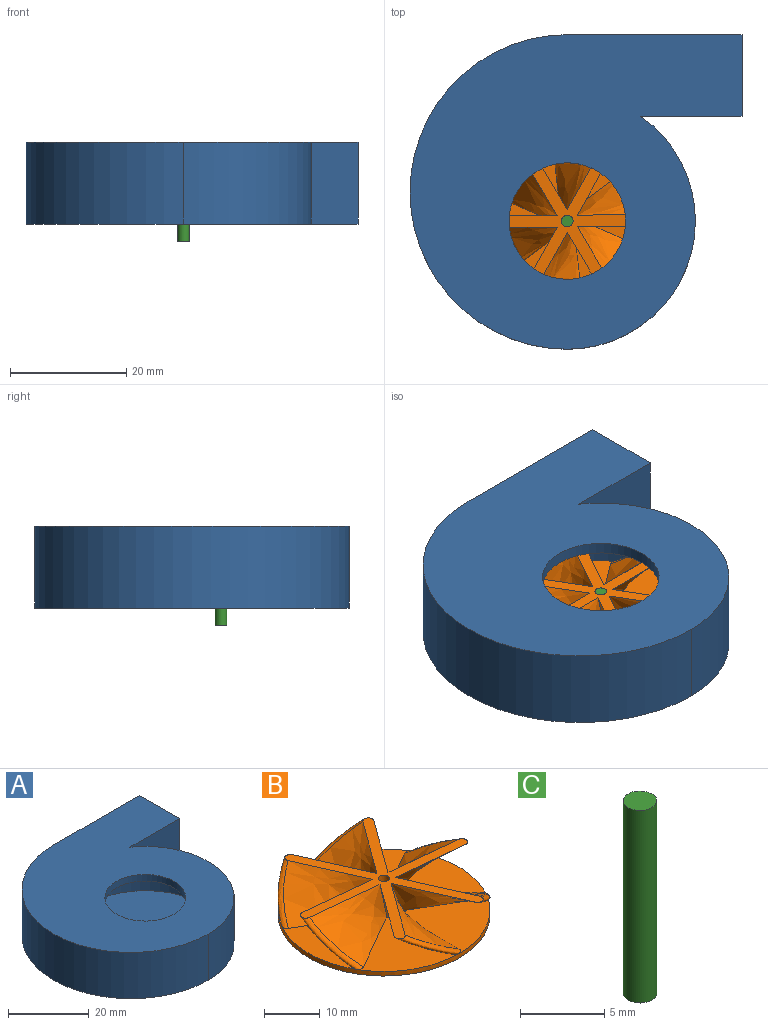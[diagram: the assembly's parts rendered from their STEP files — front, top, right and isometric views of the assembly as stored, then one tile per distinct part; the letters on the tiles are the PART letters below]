
ASSEMBLY  parts=3 mates=3
PART A: 15 faces, bbox 57x54x14 mm
  f0: plane 14x14mm, normal (1,0,0), area 96mm2, adj f2,f5,f6,f7,f8,f9,f12,f13
  f1: cylinder r=2mm len=4mm, axis (0,0,-1), area 25.1mm2, adj f7,f13
  f2: plane 30x14mm, normal (0,1,0), area 420mm2, adj f0,f3,f6,f7
  f3: cylinder r=27mm len=54mm, axis (0,0,-1), area 1187.5mm2, adj f2,f4,f6,f7
  f4: cylinder r=22mm len=40mm, axis (0,0,-1), area 778.9mm2, adj f3,f5,f6,f7
  f5: plane 17.35x14mm, normal (0,-1,0), area 242.9mm2, adj f0,f4,f6,f7
  f6: plane 57x54mm, normal (0,0,1), area 1976.8mm2, adj f0,f2,f3,f4,f5,f14
  f7: plane 57x54mm, normal (0,0,-1), area 2278.4mm2, adj f0,f1,f2,f3,f4,f5
  f8: plane 30x10mm, normal (0,1,0), area 300mm2, adj f0,f11,f12,f13
  f9: plane 30x10mm, normal (0,-1,0), area 300mm2, adj f0,f10,f12,f13
  f10: cylinder r=25mm len=50mm, axis (0,0,-1), area 785.4mm2, adj f9,f11,f12,f13
  f11: cylinder r=20mm len=40mm, axis (0,0,-1), area 628.3mm2, adj f8,f10,f12,f13
  f12: plane 55x50mm, normal (0,0,-1), area 1595.9mm2, adj f0,f8,f9,f10,f11,f14
  f13: plane 55x50mm, normal (0,0,1), area 1897.5mm2, adj f0,f1,f8,f9,f10,f11
  f14: cylinder r=10mm len=20mm, axis (0,0,-1), area 125.7mm2, adj f6,f12
PART B: 29 faces, bbox 38.3x40.7x11.3 mm
  f0: bspline ~16.86x15.64mm, area 156.6mm2, adj f1,f17,f18,f21
  f1: bspline ~12.86x7mm, area 32.7mm2, adj f0,f2,f18,f20,f21
  f2: bspline ~17.41x15.51mm, area 156.5mm2, adj f1,f3,f18,f20
  f3: bspline ~17.7x13.7mm, area 156.6mm2, adj f2,f4,f18,f20
  f4: bspline ~17.26x10mm, area 32.7mm2, adj f3,f5,f18,f20,f25
  f5: bspline ~16.5x14.45mm, area 156.5mm2, adj f4,f6,f18,f25
  f6: bspline ~15.3x15.12mm, area 156.6mm2, adj f5,f7,f18,f25
  f7: bspline ~10.15x9.3mm, area 32.7mm2, adj f6,f8,f18,f24,f25
  f8: bspline ~17.65x14.84mm, area 156.5mm2, adj f7,f9,f18,f24
  f9: bspline ~16.86x15.64mm, area 156.6mm2, adj f8,f10,f18,f24
  f10: bspline ~12.86x7mm, area 32.7mm2, adj f9,f11,f18,f23,f24
  f11: bspline ~17.41x15.51mm, area 156.5mm2, adj f10,f12,f18,f23
  f12: bspline ~17.7x13.7mm, area 156.6mm2, adj f11,f13,f18,f23
  f13: bspline ~17.26x10mm, area 32.7mm2, adj f12,f14,f18,f22,f23
  f14: bspline ~16.5x14.45mm, area 156.5mm2, adj f13,f15,f18,f22
  f15: bspline ~15.3x15.12mm, area 156.6mm2, adj f14,f16,f18,f22
  f16: bspline ~10.15x9.3mm, area 32.7mm2, adj f15,f17,f18,f21,f22
  f17: bspline ~17.65x14.84mm, area 156.5mm2, adj f0,f16,f18,f21
  f18: plane 38.1x35.18mm, normal (0,0,1), area 211.8mm2, adj f0,f1,f2,f3,f4,f5,f6,f7
  f19: bspline ~7x2mm, area 44.1mm2, adj f18,f26
  f20: plane 17.55x16.74mm, normal (0,0,1), area 153.2mm2, adj f1,f2,f3,f4,f27
  f21: plane 19.28x17.28mm, normal (0,0,1), area 153.2mm2, adj f0,f1,f16,f17,f27
  f22: plane 17.55x16.74mm, normal (0,0,1), area 153.2mm2, adj f13,f14,f15,f16,f27
  f23: plane 17.55x16.74mm, normal (0,0,1), area 153.2mm2, adj f10,f11,f12,f13,f27
  f24: plane 19.28x17.28mm, normal (0,0,1), area 153.2mm2, adj f7,f8,f9,f10,f27
  f25: plane 17.55x16.74mm, normal (0,0,1), area 153.2mm2, adj f4,f5,f6,f7,f27
  f26: cylinder r=1mm len=2mm, axis (0,0,-1), area 6.3mm2, adj f19,f28
  f27: cylinder r=19mm len=38mm, axis (0,0,-1), area 119.4mm2, adj f20,f21,f22,f23,f24,f25,f28
  f28: plane 38x38mm, normal (0,0,-1), area 1131mm2, adj f26,f27
PART C: 3 faces, bbox 2x2x14 mm
  f0: cylinder r=1mm len=14mm, axis (0,0,-1), area 88mm2, adj f1,f2
  f1: plane 2x2mm, normal (0,0,1), area 3.1mm2, adj f0
  f2: plane 2x2mm, normal (0,0,-1), area 3.1mm2, adj f0
PLACE A at identity fixed
PLACE B rot(axis=(0,0,-1),113.4deg) t=(0,0,0)mm
PLACE C rot(axis=(0,0,-1),113.4deg) t=(0,0,0)mm
MATE slider C.f0 <-> B.f26  axis (0,0,-1) through (0,0,11)mm
MATE fastened C.f0 <-> B.f26  axis (0,0,-1) through (0,0,11)mm
MATE revolute C.f0 <-> A.f1  axis (0,0,-1) through (0,0,0)mm
